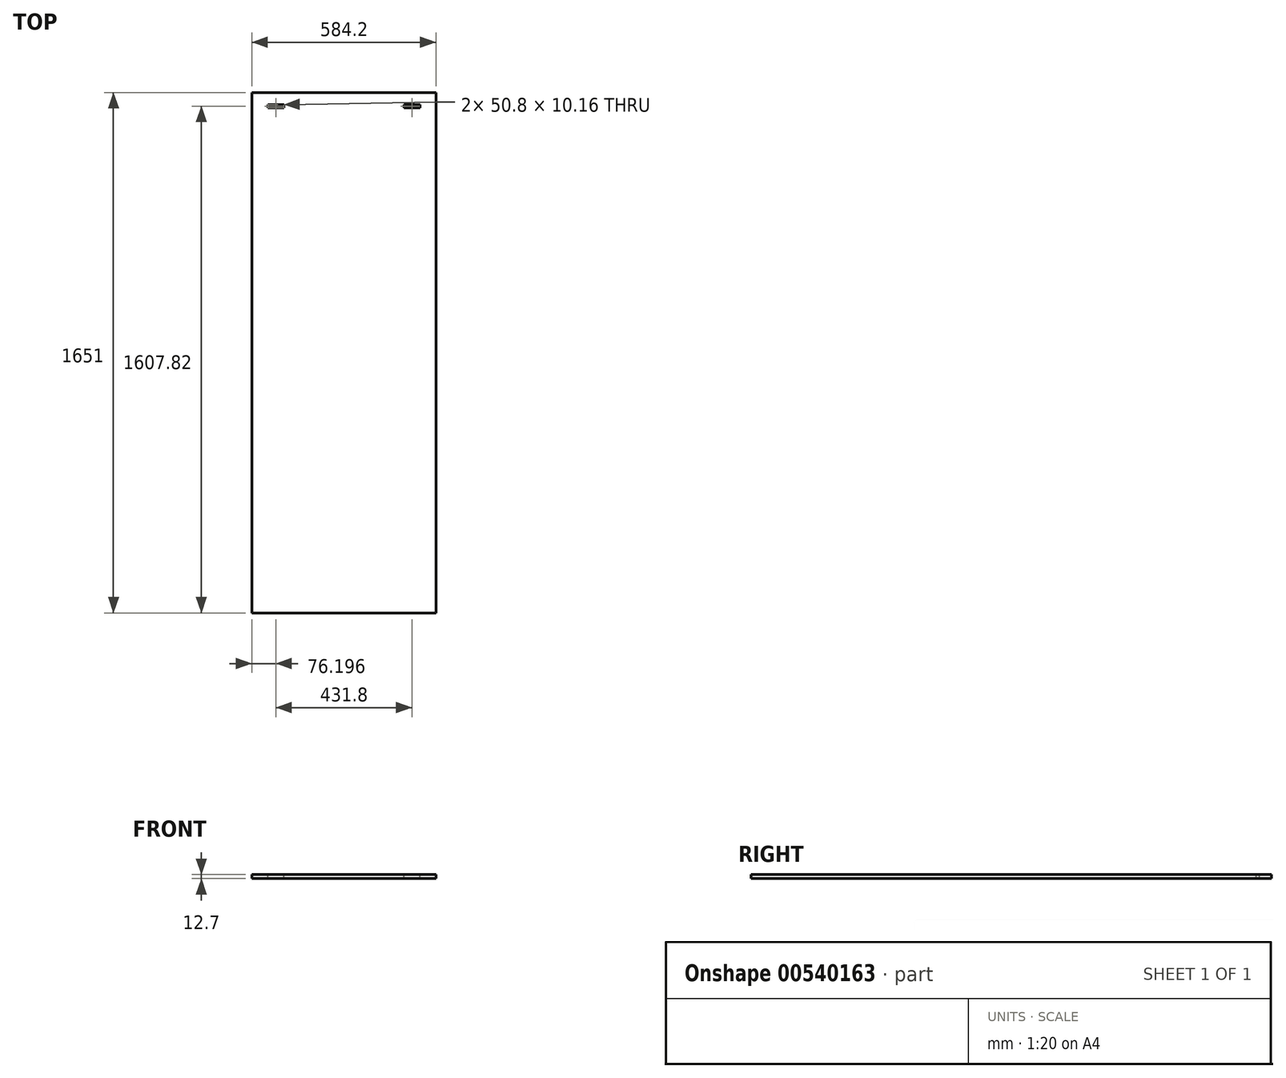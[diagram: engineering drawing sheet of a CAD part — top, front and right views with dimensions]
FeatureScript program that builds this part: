
annotation { "Feature Type Name" : "Feature", "Feature Type Description" : "" }
export const myFeature = defineFeature(function(context is Context, id is Id, definition is map)
    precondition{}
    {
        {
            var Q0;
            Q0=qCreatedBy(makeId("Top.planeOp"),FACE);
            var sketch = newSketch(context, id + "F0", { "sketchPlane" : qUnion([Q0])});
            skLineSegment(sketch, "E0.bottom", {"start": v(-311.94, 1398.71) * mm, "end": v(272.26, 1398.71) * mm});
            skLineSegment(sketch, "E0.top", {"start": v(-311.94, -252.29) * mm, "end": v(272.26, -252.29) * mm});
            skLineSegment(sketch, "E0.left", {"start": v(-311.94, 1398.71) * mm, "end": v(-311.94, -252.29) * mm});
            skLineSegment(sketch, "E0.right", {"start": v(272.26, 1398.71) * mm, "end": v(272.26, -252.29) * mm});
            skSolve(sketch);
        }
        {
            var Q0;
            Q0 = qSketchRegion(id + "F0", true);
            extrude(context, id + "F1", {"entities" : qUnion([Q0]), "oppositeDirection" : true, "depth" : 12.7 * mm, "offsetDistance" : 25.4 * mm});
        }
        {
            var Q0;
            Q0=makeQuery(id+"F1.opExtrude","CAP_FACE",FACE,{"disambiguationData":[OSD([sQuery(id+"F0.wireOp",EDGE,"E0.bottom"),sQuery(id+"F0.wireOp",EDGE,"E0.top"),sQuery(id+"F0.wireOp",EDGE,"E0.left"),sQuery(id+"F0.wireOp",EDGE,"E0.right")])],"isStart":true});
            var sketch = newSketch(context, id + "F2", { "sketchPlane" : qUnion([Q0])});
            skLineSegment(sketch, "E1.0", {"start": v(-311.94, 1360.61) * mm, "end": v(272.26, 1360.61) * mm, "construction": true});
            skLineSegment(sketch, "E2.1", {"start": v(278.6, 1125.66) * mm, "end": v(-318.3, 1125.66) * mm, "construction": true});
            skLineSegment(sketch, "E3.0", {"start": v(-261.14, 1119.31) * mm, "end": v(-261.14, -252.29) * mm, "construction": true});
            skLineSegment(sketch, "E4.0", {"start": v(221.46, 1119.31) * mm, "end": v(221.46, -252.29) * mm, "construction": true});
            skLineSegment(sketch, "E5.0", {"start": v(-311.94, 1398.71) * mm, "end": v(-311.94, -258.64) * mm, "construction": true});
            skLineSegment(sketch, "E5.1", {"start": v(272.26, 1398.71) * mm, "end": v(-311.94, 1398.71) * mm, "construction": true});
            skLineSegment(sketch, "E5.2", {"start": v(272.26, -258.64) * mm, "end": v(272.26, 1398.71) * mm, "construction": true});
            skLineSegment(sketch, "E6.bottom", {"start": v(-261.14, 1360.61) * mm, "end": v(-210.34, 1360.61) * mm});
            skLineSegment(sketch, "E6.top", {"start": v(-261.14, 1350.45) * mm, "end": v(-210.34, 1350.45) * mm});
            skLineSegment(sketch, "E6.left", {"start": v(-261.14, 1360.61) * mm, "end": v(-261.14, 1350.45) * mm});
            skLineSegment(sketch, "E6.right", {"start": v(-210.34, 1360.61) * mm, "end": v(-210.34, 1350.45) * mm});
            skLineSegment(sketch, "E7.bottom", {"start": v(221.46, 1360.61) * mm, "end": v(170.66, 1360.61) * mm});
            skLineSegment(sketch, "E7.top", {"start": v(221.46, 1350.45) * mm, "end": v(170.66, 1350.45) * mm});
            skLineSegment(sketch, "E7.left", {"start": v(221.46, 1360.61) * mm, "end": v(221.46, 1350.45) * mm});
            skLineSegment(sketch, "E7.right", {"start": v(170.66, 1360.61) * mm, "end": v(170.66, 1350.45) * mm});
            skSolve(sketch);
        }
        {
            var Q0;
            Q0=makeQuery(id+"F2.imprint","IMPRINT",FACE,{"disambiguationData":[TD([[makeQuery(id+"F2.imprint","IMPRINT",EDGE,{"derivedFrom":sQuery(id+"F2.wireOp",EDGE,"E6.bottom")}),-1.0]])]});
            var Q1;
            Q1=makeQuery(id+"F2.imprint","IMPRINT",FACE,{"disambiguationData":[TD([[makeQuery(id+"F2.imprint","IMPRINT",EDGE,{"derivedFrom":sQuery(id+"F2.wireOp",EDGE,"E7.bottom")}),1.0]])]});
            extrude(context, id + "F3", {"entities" : qUnion([Q0, Q1]), "operationType" : NewBodyOperationType.REMOVE, "oppositeDirection" : true, "depth" : 15.24 * mm, "offsetDistance" : 25.4 * mm});
        }
    });
